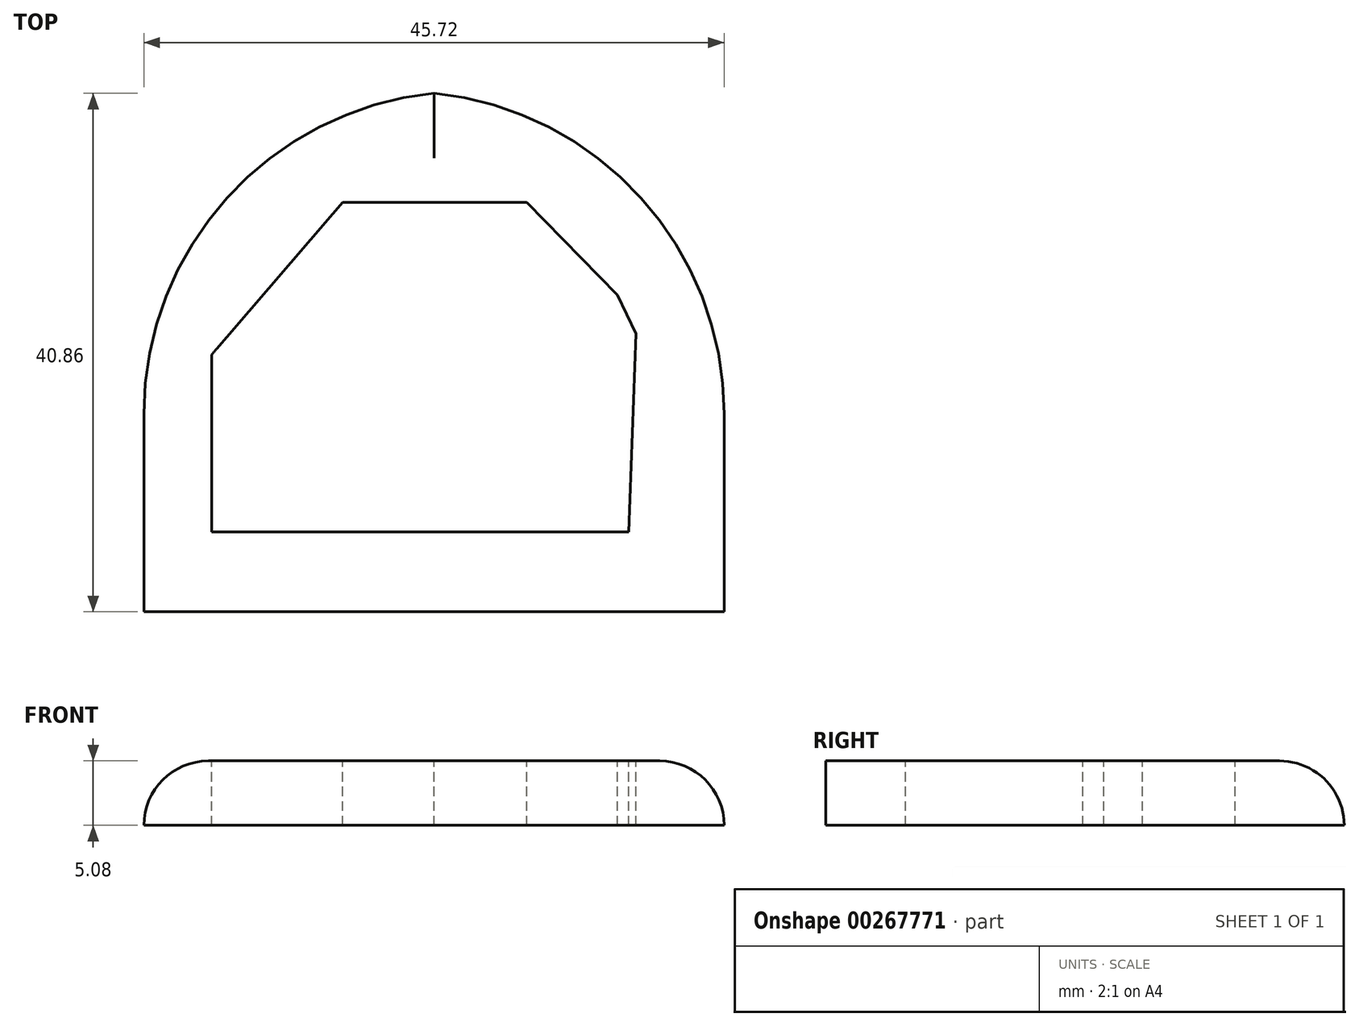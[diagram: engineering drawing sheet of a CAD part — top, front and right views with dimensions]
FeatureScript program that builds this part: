
annotation { "Feature Type Name" : "Feature", "Feature Type Description" : "" }
export const myFeature = defineFeature(function(context is Context, id is Id, definition is map)
    precondition{}
    {
        {
            var Q0;
            Q0=qCreatedBy(makeId("Top.planeOp"),FACE);
            var sketch = newSketch(context, id + "F0", { "sketchPlane" : qUnion([Q0])});
            skLineSegment(sketch, "E0.bottom", {"start": v(0, 0) * mm, "end": v(45.72, 0) * mm});
            skLineSegment(sketch, "E0.top", {"start": v(0, 41) * mm, "end": v(45.72, 41) * mm});
            skLineSegment(sketch, "E0.left", {"start": v(0, 0) * mm, "end": v(0, 41) * mm});
            skLineSegment(sketch, "E0.right", {"start": v(45.72, 0) * mm, "end": v(45.72, 41) * mm});
            skSolve(sketch);
        }
        {
            var Q0;
            Q0=makeQuery(id+"F0.imprint","IMPRINT",FACE,{"disambiguationData":[TD([[makeQuery(id+"F0.imprint","IMPRINT",EDGE,{"derivedFrom":sQuery(id+"F0.wireOp",EDGE,"E0.bottom")}),1.0]])]});
            extrude(context, id + "F1", {"entities" : qUnion([Q0]), "depth" : 5.08 * mm});
        }
        {
            var Q0;
            Q0=makeQuery(id+"F1.opExtrude","SWEPT_EDGE",EDGE,{"disambiguationData":[OSD([sQuery(id+"F0.wireOp",EDGE,"E0.top"),sQuery(id+"F0.wireOp",EDGE,"E0.left")])]});
            var Q1;
            Q1=makeQuery(id+"F1.opExtrude","SWEPT_EDGE",EDGE,{"disambiguationData":[OSD([sQuery(id+"F0.wireOp",EDGE,"E0.top"),sQuery(id+"F0.wireOp",EDGE,"E0.right")])]});
            fillet(context, id + "F2", {"entities" : qUnion([Q0, Q1]), "radius" : 25.4 * mm, "tangentPropagation" : true, "allowEdgeOverflow" : false});
        }
        {
            var Q0;
            Q0=makeQuery(id+"F1.opExtrude","CAP_FACE",FACE,{"disambiguationData":[OSD([sQuery(id+"F0.wireOp",EDGE,"E0.bottom"),sQuery(id+"F0.wireOp",EDGE,"E0.top"),sQuery(id+"F0.wireOp",EDGE,"E0.left"),sQuery(id+"F0.wireOp",EDGE,"E0.right")])],"isStart":false});
            var sketch = newSketch(context, id + "F3", { "sketchPlane" : qUnion([Q0])});
            skLineSegment(sketch, "E1", {"start": v(38.21, 6.3) * mm, "end": v(5.34, 6.3) * mm});
            skLineSegment(sketch, "E2", {"start": v(5.34, 6.3) * mm, "end": v(5.34, 20.27) * mm});
            skLineSegment(sketch, "E3", {"start": v(5.34, 20.27) * mm, "end": v(15.66, 32.27) * mm});
            skLineSegment(sketch, "E4", {"start": v(15.66, 32.27) * mm, "end": v(22.3, 32.27) * mm});
            skLineSegment(sketch, "E5", {"start": v(22.3, 32.27) * mm, "end": v(30.15, 32.27) * mm});
            skLineSegment(sketch, "E6", {"start": v(30.15, 32.27) * mm, "end": v(37.32, 24.98) * mm});
            skLineSegment(sketch, "E7", {"start": v(37.32, 24.98) * mm, "end": v(38.76, 21.9) * mm});
            skLineSegment(sketch, "E8", {"start": v(38.76, 21.9) * mm, "end": v(38.21, 6.3) * mm});
            skSolve(sketch);
        }
        {
            var Q0;
            Q0=makeQuery(id+"F3.imprint","IMPRINT",FACE,{"disambiguationData":[TD([[makeQuery(id+"F3.imprint","IMPRINT",EDGE,{"derivedFrom":sQuery(id+"F3.wireOp",EDGE,"E1")}),-1.0]])]});
            extrude(context, id + "F4", {"entities" : qUnion([Q0]), "operationType" : NewBodyOperationType.REMOVE, "oppositeDirection" : true, "depth" : 25.4 * mm});
        }
        {
            var Q0;
            {var subQ0=sQuery(id+"F0.wireOp",EDGE,"E0.right");var subQ1=sQuery(id+"F0.wireOp",EDGE,"E0.top");Q0=makeQuery(id+"F2.opFillet","BLEND_EDGE",EDGE,{"blendedFrom":[makeQuery(id+"F1.opExtrude","SWEPT_EDGE",EDGE,{"disambiguationData":[OSD([subQ1,subQ0])]}),makeQuery(id+"F1.opExtrude","CAP_FACE",FACE,{"disambiguationData":[OSD([sQuery(id+"F0.wireOp",EDGE,"E0.bottom"),subQ1,sQuery(id+"F0.wireOp",EDGE,"E0.left"),subQ0])],"isStart":false})],"blendedInto":[makeQuery(id+"F1.opExtrude","CAP_FACE",FACE,{"disambiguationData":[OSD([sQuery(id+"F0.wireOp",EDGE,"E0.bottom"),subQ1,sQuery(id+"F0.wireOp",EDGE,"E0.left"),subQ0])],"isStart":false})]});}
            var Q1;
            {var subQ0=sQuery(id+"F0.wireOp",EDGE,"E0.left");var subQ1=sQuery(id+"F0.wireOp",EDGE,"E0.top");Q1=makeQuery(id+"F2.opFillet","BLEND_EDGE",EDGE,{"blendedFrom":[makeQuery(id+"F1.opExtrude","SWEPT_EDGE",EDGE,{"disambiguationData":[OSD([subQ1,subQ0])]}),makeQuery(id+"F1.opExtrude","CAP_FACE",FACE,{"disambiguationData":[OSD([sQuery(id+"F0.wireOp",EDGE,"E0.bottom"),subQ1,subQ0,sQuery(id+"F0.wireOp",EDGE,"E0.right")])],"isStart":false})],"blendedInto":[makeQuery(id+"F1.opExtrude","CAP_FACE",FACE,{"disambiguationData":[OSD([sQuery(id+"F0.wireOp",EDGE,"E0.bottom"),subQ1,subQ0,sQuery(id+"F0.wireOp",EDGE,"E0.right")])],"isStart":false})]});}
            fillet(context, id + "F5", {"entities" : qUnion([Q0, Q1]), "radius" : 5.08 * mm, "tangentPropagation" : true, "allowEdgeOverflow" : false});
        }
    });
